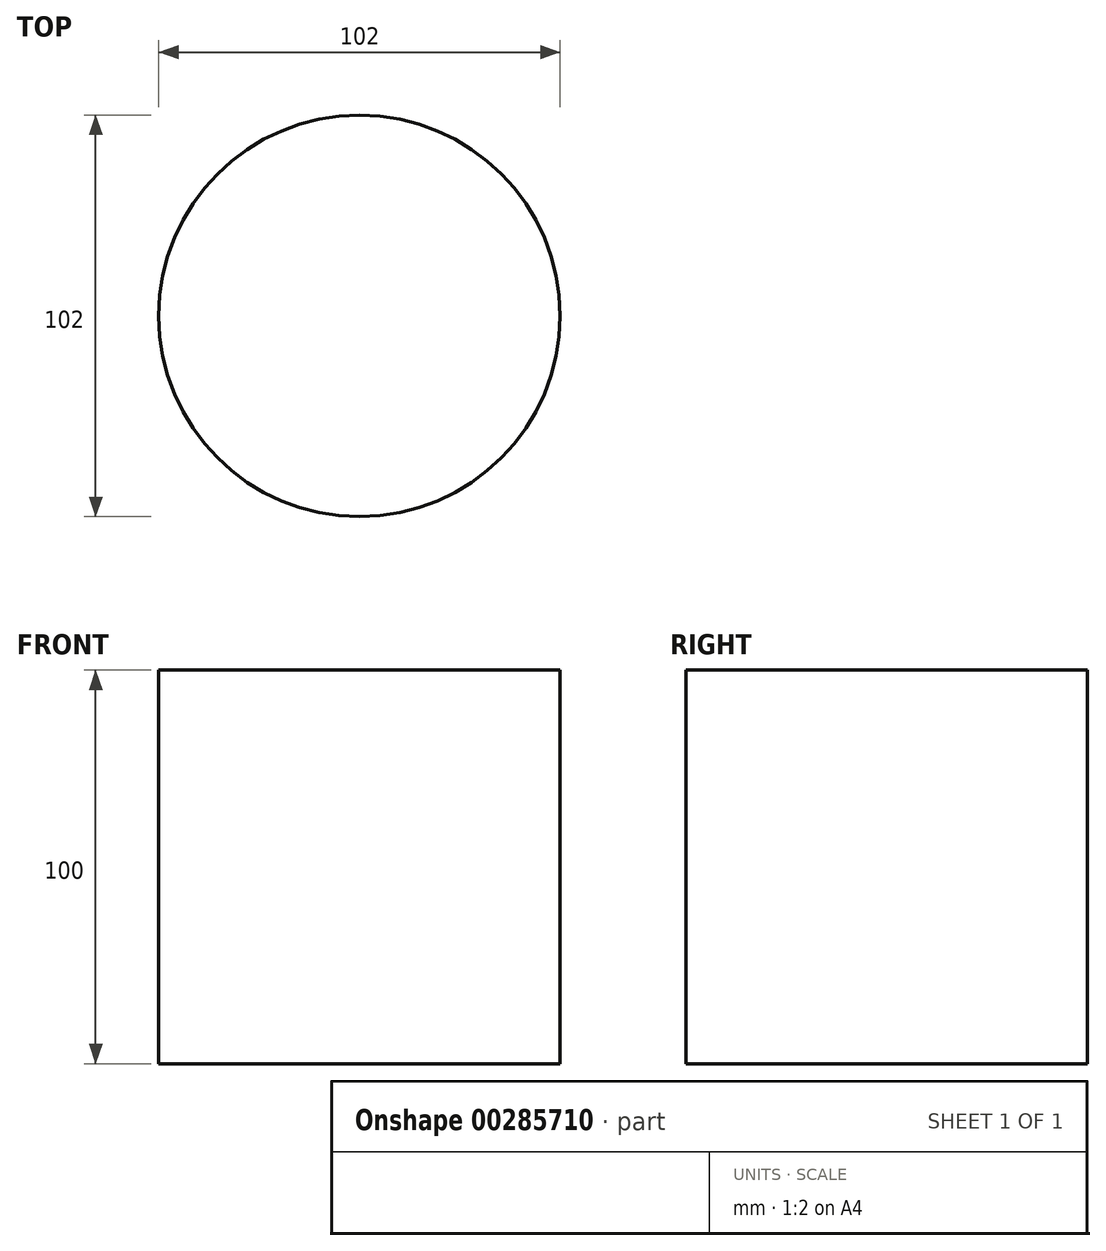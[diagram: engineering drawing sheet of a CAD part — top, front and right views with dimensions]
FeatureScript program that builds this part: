
annotation { "Feature Type Name" : "Feature", "Feature Type Description" : "" }
export const myFeature = defineFeature(function(context is Context, id is Id, definition is map)
    precondition{}
    {
        {
            var Q0;
            Q0=qCreatedBy(makeId("Top.planeOp"),FACE);
            var sketch = newSketch(context, id + "F0", { "sketchPlane" : qUnion([Q0])});
            skCircle(sketch, "E0", {"center": v(0, 0) * mm, "radius": 51 * mm});
            skSolve(sketch);
        }
        {
            var Q0;
            Q0=makeQuery(id+"F0.imprint","IMPRINT",FACE,{"disambiguationData":[TD([[makeQuery(id+"F0.imprint","IMPRINT",EDGE,{"derivedFrom":sQuery(id+"F0.wireOp",EDGE,"E0")}),1.0]])]});
            extrude(context, id + "F1", {"entities" : qUnion([Q0]), "depth" : 100 * mm});
        }
    });
